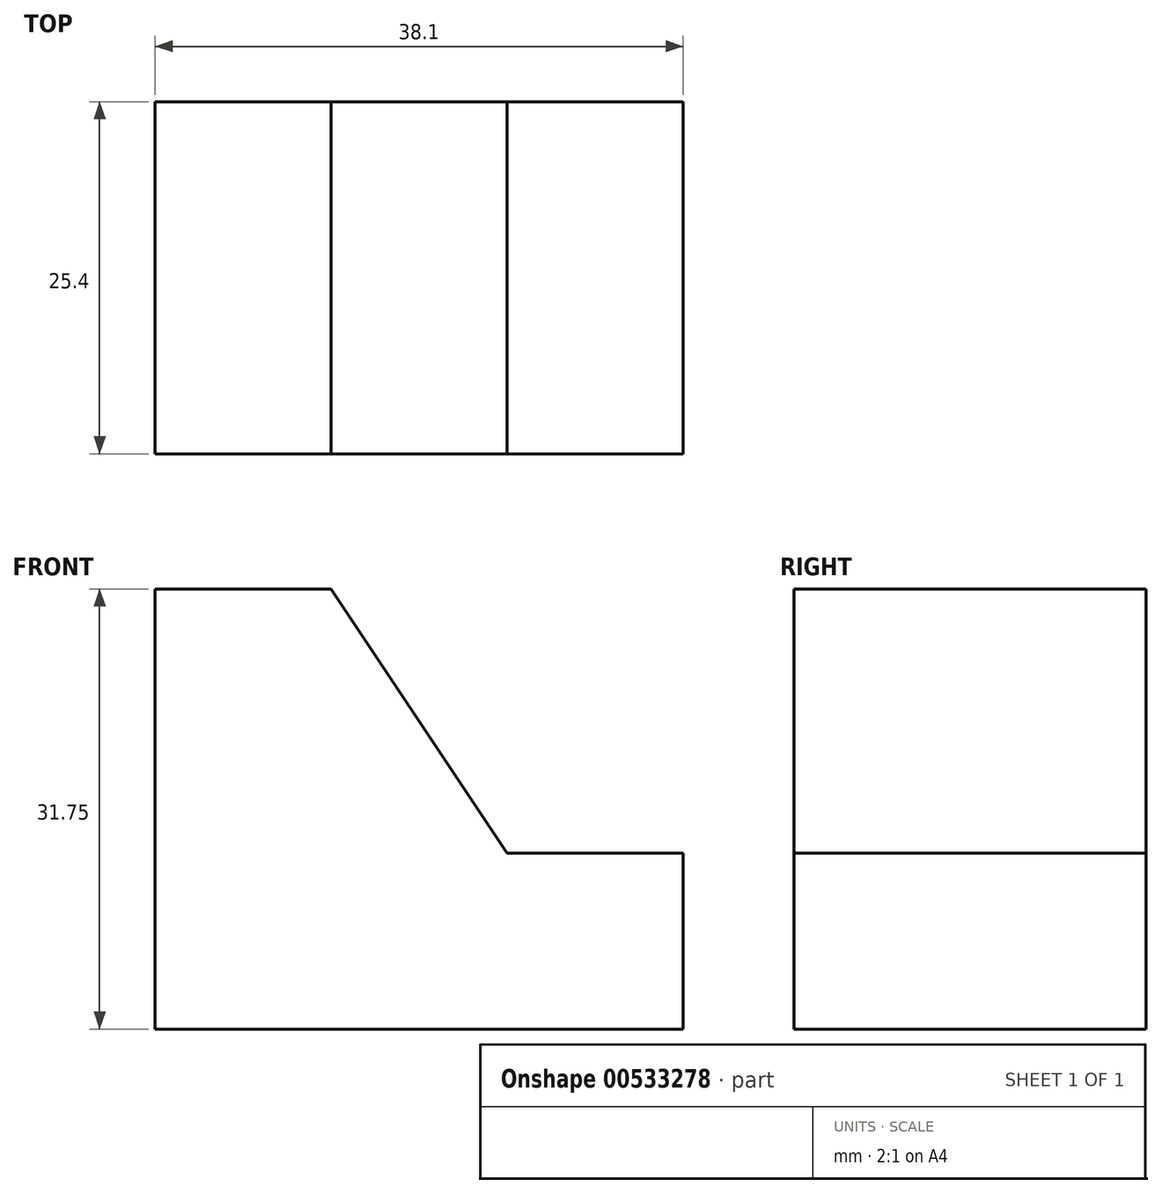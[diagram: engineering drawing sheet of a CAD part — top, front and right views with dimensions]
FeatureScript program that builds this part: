
annotation { "Feature Type Name" : "Feature", "Feature Type Description" : "" }
export const myFeature = defineFeature(function(context is Context, id is Id, definition is map)
    precondition{}
    {
        {
            var Q0;
            Q0=qCreatedBy(makeId("Front.planeOp"),FACE);
            var sketch = newSketch(context, id + "F0", { "sketchPlane" : qUnion([Q0])});
            skLineSegment(sketch, "E0", {"start": v(-55.65, 44.43) * mm, "end": v(-42.95, 44.43) * mm});
            skLineSegment(sketch, "E1", {"start": v(-42.95, 44.43) * mm, "end": v(-30.25, 25.38) * mm});
            skLineSegment(sketch, "E2", {"start": v(-30.25, 25.38) * mm, "end": v(-17.55, 25.38) * mm});
            skLineSegment(sketch, "E3", {"start": v(-17.55, 25.38) * mm, "end": v(-17.55, 12.68) * mm});
            skLineSegment(sketch, "E4", {"start": v(-17.55, 12.68) * mm, "end": v(-55.65, 12.68) * mm});
            skLineSegment(sketch, "E5", {"start": v(-55.65, 12.68) * mm, "end": v(-55.65, 44.43) * mm});
            skSolve(sketch);
        }
        {
            var Q0;
            Q0 = qSketchRegion(id + "F0", true);
            extrude(context, id + "F1", {"entities" : qUnion([Q0]), "depth" : 25.4 * mm, "offsetDistance" : 25.4 * mm});
        }
    });
